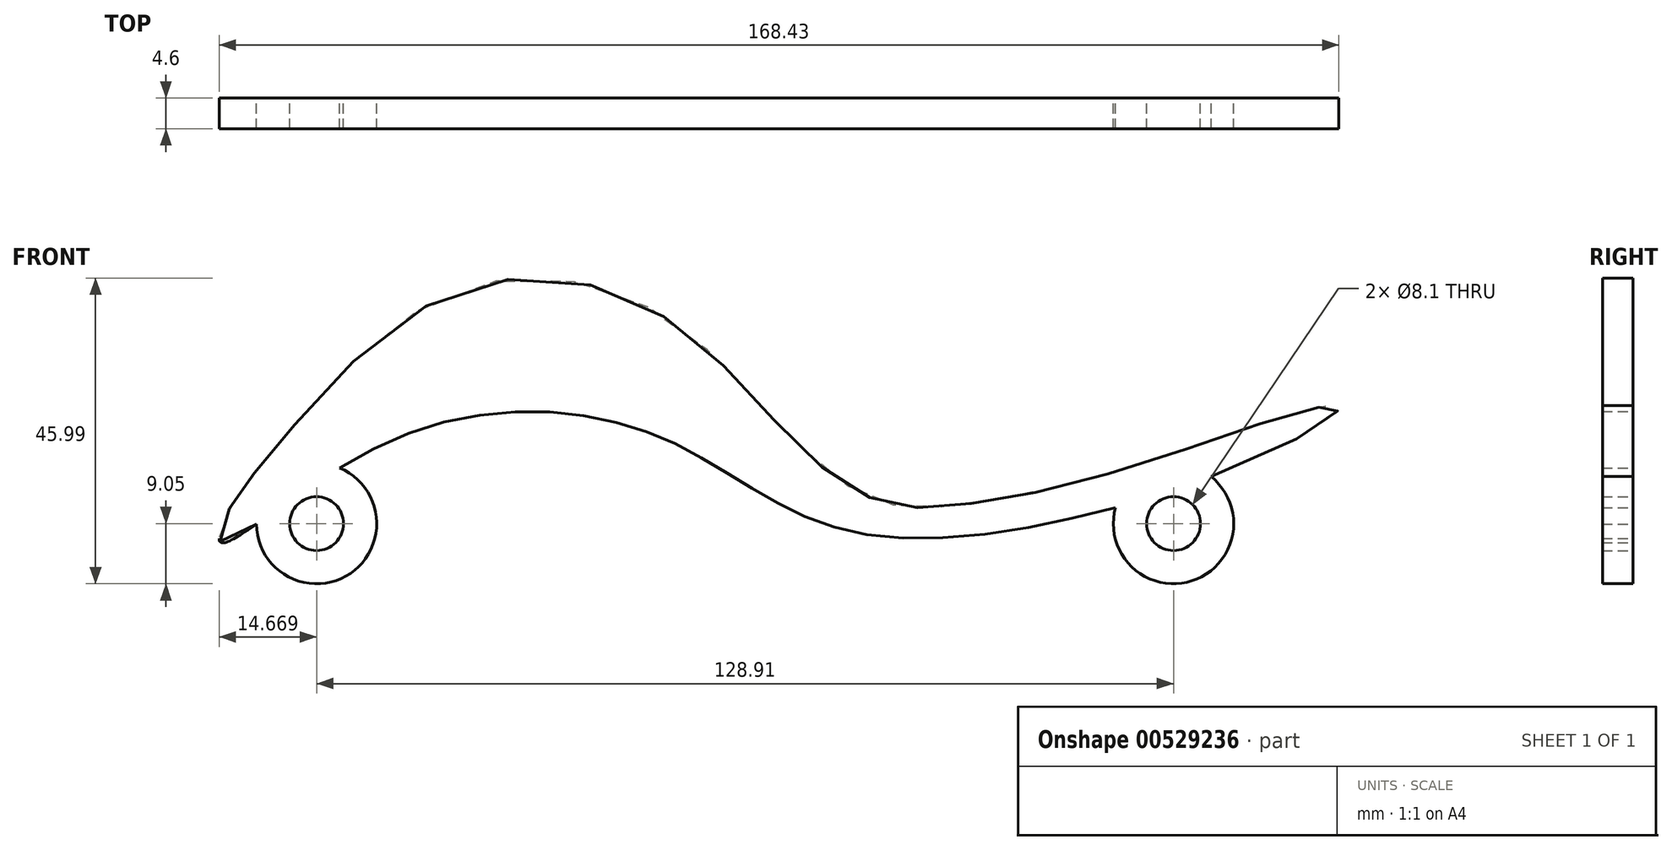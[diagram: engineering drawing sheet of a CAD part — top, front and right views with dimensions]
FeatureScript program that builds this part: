
annotation { "Feature Type Name" : "Feature", "Feature Type Description" : "" }
export const myFeature = defineFeature(function(context is Context, id is Id, definition is map)
    precondition{}
    {
        {
            var Q0;
            Q0=qCreatedBy(makeId("Front.planeOp"),FACE);
            var sketch = newSketch(context, id + "F0", { "sketchPlane" : qUnion([Q0])});
            skLineSegment(sketch, "E0", {"start": v(-102.58, 0) * mm, "end": v(64.9, 0) * mm, "construction": true});
            skCircle(sketch, "E1", {"center": v(-86.6, 9.15) * mm, "radius": 4.05 * mm});
            skArc(sketch, "E2.0", {"start": v(-95.65, 9.06) * mm, "mid": v(-81.52, 1.66) * mm, "end": v(-83.17, 17.53) * mm});
            skCircle(sketch, "E3", {"center": v(42.3, 9.15) * mm, "radius": 4.05 * mm});
            skArc(sketch, "E4.0", {"start": v(33.6, 11.58) * mm, "mid": v(45.1, 0.54) * mm, "end": v(47.96, 16.22) * mm});
            skFitSpline(sketch, "E5", {"points": [v(-100.99, 6.33) * mm, v(-75.6, 21.56) * mm, v(-34.13, 21.84) * mm, v(-3.67, 7.46) * mm, v(56.13, 19.59) * mm, v(67.13, 26.64) * mm, v(60.64, 25.8) * mm, v(33, 16.77) * mm, v(10.15, 11.97) * mm, v(-2.17, 12.57) * mm, v(-15.93, 22.77) * mm, v(-36.33, 41.5) * mm, v(-67.64, 43.17) * mm, v(-93.5, 19.69) * mm, v(-99.86, 11.12) * mm, v(-100.99, 6.33) * mm]});
            skSolve(sketch);
        }
        {
            var Q0;
            Q0 = qSketchRegion(id + "F0", true);
            extrude(context, id + "F1", {"entities" : qUnion([Q0]), "depth" : 4.6 * mm, "offsetDistance" : 25 * mm});
        }
    });
